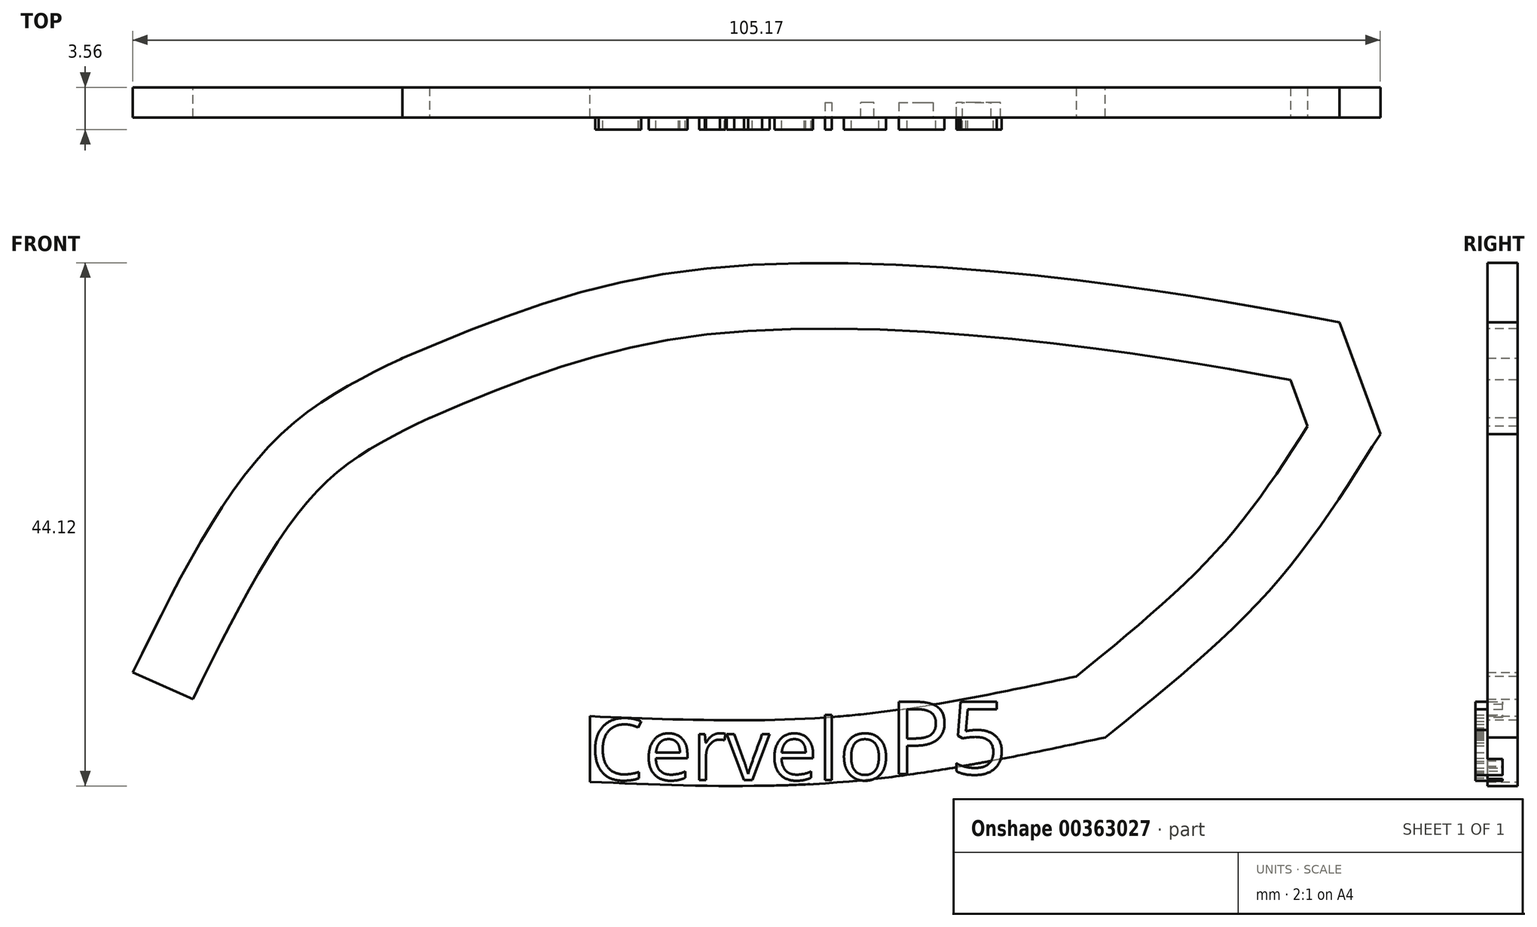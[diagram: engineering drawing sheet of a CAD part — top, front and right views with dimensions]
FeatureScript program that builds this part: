
annotation { "Feature Type Name" : "Feature", "Feature Type Description" : "" }
export const myFeature = defineFeature(function(context is Context, id is Id, definition is map)
    precondition{}
    {
        {
            var Q0;
            Q0=qCreatedBy(makeId("Right.planeOp"),FACE);
            var sketch = newSketch(context, id + "F0", { "sketchPlane" : qUnion([Q0])});
            skLineSegment(sketch, "E0.bottom", {"start": v(-1.27, 2.77) * mm, "end": v(1.27, 2.77) * mm});
            skLineSegment(sketch, "E0.top", {"start": v(-1.27, -2.77) * mm, "end": v(1.27, -2.77) * mm});
            skLineSegment(sketch, "E0.left", {"start": v(-1.27, 2.77) * mm, "end": v(-1.27, -2.77) * mm});
            skLineSegment(sketch, "E0.right", {"start": v(1.27, 2.77) * mm, "end": v(1.27, -2.77) * mm});
            skPoint(sketch, "E0.middle", {"position": v(0, 0) * mm});
            skSolve(sketch);
        }
        {
            var Q0;
            Q0=qCreatedBy(makeId("Front.planeOp"),FACE);
            var sketch = newSketch(context, id + "F1", { "sketchPlane" : qUnion([Q0])});
            skFitSpline(sketch, "E1", {"points": [v(0, 0) * mm, v(21.34, 0) * mm, v(42.23, 3.56) * mm], "startDerivative": vector(42.79, -1.78) * mm, "endDerivative": vector(41.67, 8.9) * mm});
            skFitSpline(sketch, "E2", {"points": [v(42.23, 3.56) * mm, v(55.12, 15.11) * mm, v(63.56, 26.9) * mm], "startDerivative": vector(26.52, 21.47) * mm, "endDerivative": vector(16, 25.26) * mm});
            skLineSegment(sketch, "E3", {"start": v(63.56, 26.9) * mm, "end": v(61.12, 33.56) * mm});
            skFitSpline(sketch, "E4", {"points": [v(61.12, 33.56) * mm, v(41.78, 36.67) * mm, v(8.22, 37.56) * mm, v(-14.67, 30.45) * mm], "startDerivative": vector(-59.93, 11.03) * mm, "endDerivative": vector(-64.98, -27.4) * mm});
            skFitSpline(sketch, "E5", {"points": [v(-14.67, 30.45) * mm, v(-24.9, 23.78) * mm, v(-36, 5.33) * mm], "startDerivative": vector(-24.73, -11.91) * mm, "endDerivative": vector(-18.24, -37.13) * mm});
            skLineSegment(sketch, "E6", {"start": v(-1.37, 0) * mm, "end": v(0, 35.07) * mm});
            skSolve(sketch);
        }
        {
            var Q0;
            Q0=makeQuery(id+"F0.imprint","IMPRINT",FACE,{"disambiguationData":[TD([[makeQuery(id+"F0.imprint","IMPRINT",EDGE,{"derivedFrom":sQuery(id+"F0.wireOp",EDGE,"E0.bottom")}),-1.0]])]});
            var Q1;
            Q1=sQuery(id+"F1.wireOp",EDGE,"E1");
            var Q2;
            Q2=sQuery(id+"F1.wireOp",EDGE,"E2");
            var Q3;
            Q3=sQuery(id+"F1.wireOp",EDGE,"E3");
            var Q4;
            Q4=sQuery(id+"F1.wireOp",EDGE,"E4");
            var Q5;
            Q5=sQuery(id+"F1.wireOp",EDGE,"E5");
            sweep(context, id + "F2", {"profiles" : qUnion([Q0]), "path" : qUnion([Q1, Q2, Q3, Q4, Q5])});
        }
        {
            var Q0;
            Q0=qCreatedBy(makeId("Front.planeOp"),FACE);
            var sketch = newSketch(context, id + "F3", { "sketchPlane" : qUnion([Q0])});
            skText(sketch, "E7", { "text": "Cervelo", "fontName": "OpenSans-Regular.ttf"});
            const initialGuessF3  = {"E7": [0, -0.0026, 1, 0, 0.00519]};
            skSetInitialGuess(sketch, initialGuessF3);
            skSolve(sketch);
        }
        {
            var Q0;
            Q0 = qSketchRegion(id + "F3", true);
            extrude(context, id + "F4", {"entities" : qUnion([Q0]), "operationType" : NewBodyOperationType.ADD, "depth" : 2.3 * mm});
        }
        {
            var Q0;
            Q0=qCreatedBy(makeId("Front.planeOp"),FACE);
            var sketch = newSketch(context, id + "F5", { "sketchPlane" : qUnion([Q0])});
            skText(sketch, "E8", { "text": "P5", "fontName": "OpenSans-Regular.ttf"});
            const initialGuessF5  = {"E8": [0.0252, -0.00211, 1, 0, 0.00614]};
            skSetInitialGuess(sketch, initialGuessF5);
            skSolve(sketch);
        }
        {
            var Q0;
            Q0 = qSketchRegion(id + "F5", true);
            extrude(context, id + "F6", {"entities" : qUnion([Q0]), "operationType" : NewBodyOperationType.ADD, "depth" : 2.3 * mm});
        }
    });
